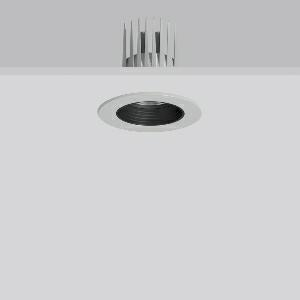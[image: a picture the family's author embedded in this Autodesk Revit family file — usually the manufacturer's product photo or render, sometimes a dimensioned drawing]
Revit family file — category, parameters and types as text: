
# Revit family: heledon_mini_e_901747_004_3_76_428d
name_source: partatom
category: Lighting Fixtures
units: mm (PartAtom-declared; Revit-internal decimal feet)

## family parameters
Cut with Voids When Loaded = No
Host = Face
Light Source = No
Part Type = Normal
Room Calculation Point = No
Round Connector Dimension = Use Diameter
Shared = No

## types (1)
- HELEDON mini E (1 x LED Modul 935, 1950 lm, 3500)
    Apparent Load = 20 VA
    Approval mark = CE
    CIE Flux Codes = 95 100 100 100 100
    Color Rendering = 92
    Color Temperature = 3500
    Default Elevation = 1800 mm
    Description = Series: HELEDON mini
Round recessed downlight. Housing: die-cast aluminium, powder-coated. Black plastic ring and recessed LED to prevent glare from the side. Optical assembly with lens made of plastic (polycarbonate) for the best homogeneous light distribution - can be changed without tools. Best colour rendering index Ra>90. Suitable for Recessed ceiling mounting. Installation without tools thanks to spring fastening system. Including separate LED converter with connecting cable 600 mm.High quality converter without flickering and stroboscopic effect. Through-wiring box (5 pole) available as accessory. The following accessories can be mounted without use of tools: interchangeable lenses, decorative glasses, honeycomb louvre, clear and frosted diffusers, white interchangeable plastic ring. 
Colour: silver
Diameter: 124 mm
Height: 3 mm
Cut-out diameter: 114 mm
Recess height: 170 mm
Luminaire: recess height: 120 mm
Lamp: LED
Socket: without socket
Colour temperature: 3500K
Colour rendering index (CRI): 92
System power: 20 W
Rated luminous flux: 1950 lm
Luminous efficiency: 98 lm/W
Control gear: Converter, dimmable, DALI
Protection class: II
Type of protection: IP 20
    Height = 0 mm  [stored 0 ft]
    Lamp = 1 x LED Modul 935
    Lamp Light Flux = 1950 lm
    Lamp count = 1
    Length = 124 mm  [stored 0.406824 ft]
    Lifetime = 50000 h
    Luminous efficacy = 98 lm/W
    Manufacturer = RZB
    ModVariant = No
    Model = 901747.004.3.76
    Mounting Place = Ceiling
    Mounting Type = Recessed
    Number of Poles = 1
    OnlyDefault = Yes
    Power Factor = 1
    Product Name = HELEDON mini E
    Product group = Recessed downlights
    ProductGroupID = 402
    Protection Class = Protection class II
    Protection Degree = IP 20
    RLX_Detail_Level = 1
    RLX_Emergency_Light_Flux = 0 lm
    RLX_Emergency_Type = 0
    RLX_Emergency_Type_DB = No
    RlxData = <blob elided: 134973 chars, md5=0d76da79>
    Socket = socket
    Standby Power = 0 W
    System Light Flux = 1950 lm
    System Power = 20 W
    Type Comments = Product without accessories
    Type Image = 901656.004.jpg
    URL = http://relux.com
    VarID = ---
    Voltage = 230 V
    Voltage Range = 220-240 V
    Weight = 0.00 kg
    Width = 0 mm  [stored 0 ft]

note: [stored X ft] marks values corroborated as IEEE doubles in the binary element streams (Revit-internal decimal feet)

## geometry (parser evidence)
native form markers: Blend x4, Sweep x9
no freeform markers — native parametric forms only
